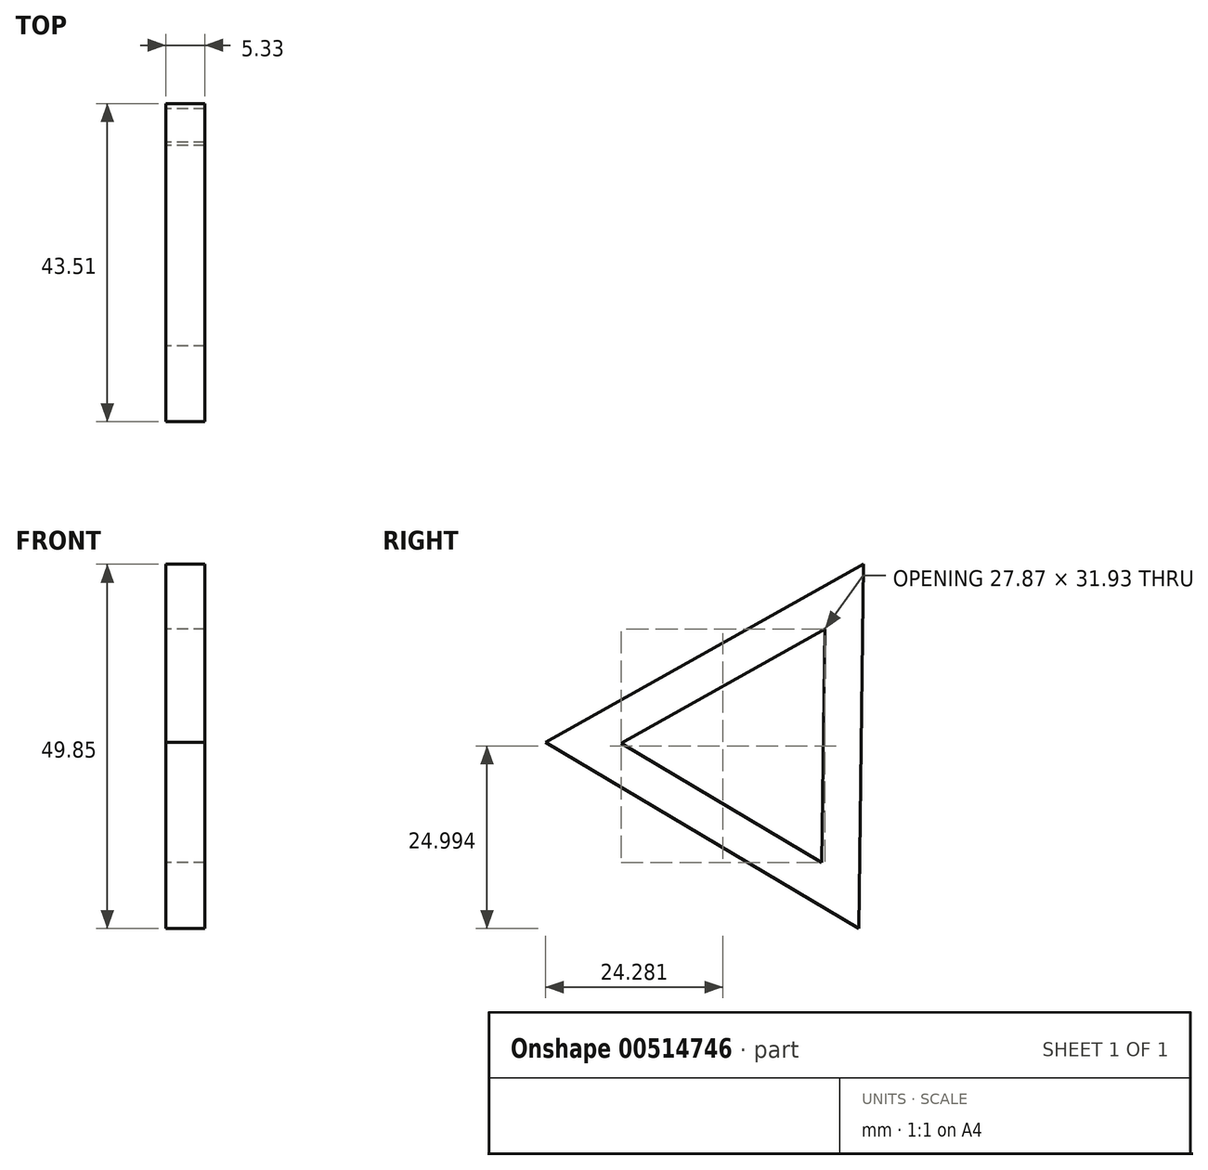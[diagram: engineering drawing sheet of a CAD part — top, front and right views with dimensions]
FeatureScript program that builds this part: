
annotation { "Feature Type Name" : "Feature", "Feature Type Description" : "" }
export const myFeature = defineFeature(function(context is Context, id is Id, definition is map)
    precondition{}
    {
        {
            var Q0;
            Q0=qCreatedBy(makeId("Right.planeOp"),FACE);
            var sketch = newSketch(context, id + "F0", { "sketchPlane" : qUnion([Q0])});
            skCircle(sketch, "E0.cCircle", {"center": v(0, 0) * mm, "radius": 9.22 * mm, "construction": true});
            skLineSegment(sketch, "E0.0", {"start": v(-18.43, 0.25) * mm, "end": v(9.43, 15.84) * mm});
            skLineSegment(sketch, "E0.1", {"start": v(9.43, 15.84) * mm, "end": v(9, -16.09) * mm});
            skLineSegment(sketch, "E0.2", {"start": v(9, -16.09) * mm, "end": v(-18.43, 0.25) * mm});
            skPoint(sketch, "E0.0.midPoint", {"position": v(-4.5, 8.04) * mm});
            skCircle(sketch, "E1.cCircle", {"center": v(0, 0) * mm, "radius": 14.4 * mm, "construction": true});
            skLineSegment(sketch, "E1.0", {"start": v(-28.78, 0.4) * mm, "end": v(14.73, 24.73) * mm});
            skLineSegment(sketch, "E1.1", {"start": v(14.73, 24.73) * mm, "end": v(14.05, -25.12) * mm});
            skLineSegment(sketch, "E1.2", {"start": v(14.05, -25.12) * mm, "end": v(-28.78, 0.4) * mm});
            skPoint(sketch, "E1.0.midPoint", {"position": v(-7.03, 12.56) * mm});
            skSolve(sketch);
        }
        {
            var Q0;
            Q0 = qSketchRegion(id + "F0", true);
            extrude(context, id + "F1", {"entities" : qUnion([Q0]), "depth" : 5.33 * mm, "offsetDistance" : 25.4 * mm});
        }
    });
